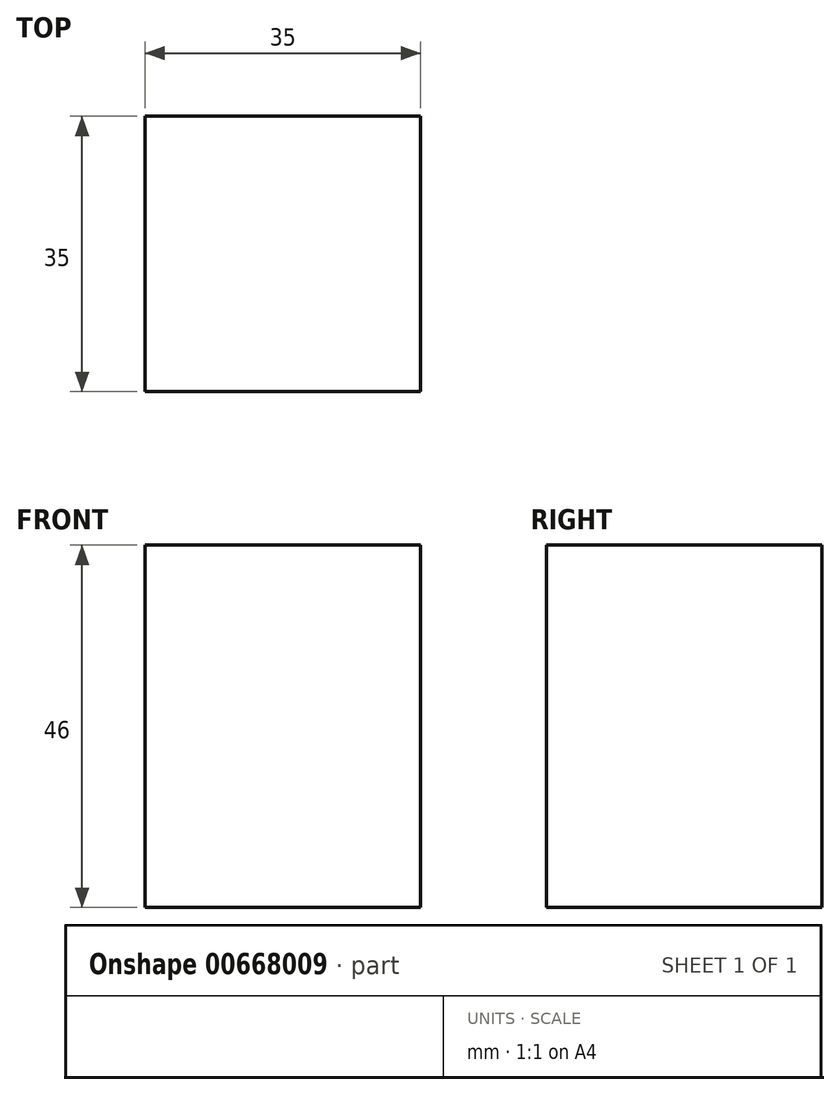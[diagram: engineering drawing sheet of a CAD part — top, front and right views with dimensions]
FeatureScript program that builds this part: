
annotation { "Feature Type Name" : "Feature", "Feature Type Description" : "" }
export const myFeature = defineFeature(function(context is Context, id is Id, definition is map)
    precondition{}
    {
        {
            var Q0;
            Q0=qCreatedBy(makeId("Front.planeOp"),FACE);
            var sketch = newSketch(context, id + "F0", { "sketchPlane" : qUnion([Q0])});
            skLineSegment(sketch, "E0.top", {"start": v(-20.43, 34.05) * mm, "end": v(14.57, 34.05) * mm});
            skLineSegment(sketch, "E0.left", {"start": v(-20.43, -11.95) * mm, "end": v(-20.43, 34.05) * mm});
            skLineSegment(sketch, "E1", {"start": v(14.57, 34.05) * mm, "end": v(14.57, -11.95) * mm});
            skLineSegment(sketch, "E2", {"start": v(-20.43, -11.95) * mm, "end": v(14.57, -11.95) * mm});
            skSolve(sketch);
        }
        {
            var Q0;
            Q0=makeQuery(id+"F0.imprint","IMPRINT",FACE,{"disambiguationData":[TD([[makeQuery(id+"F0.imprint","IMPRINT",EDGE,{"derivedFrom":sQuery(id+"F0.wireOp",EDGE,"E0.top")}),-1.0]])]});
            extrude(context, id + "F1", {"entities" : qUnion([Q0]), "depth" : 35 * mm, "offsetDistance" : 25 * mm});
        }
    });
